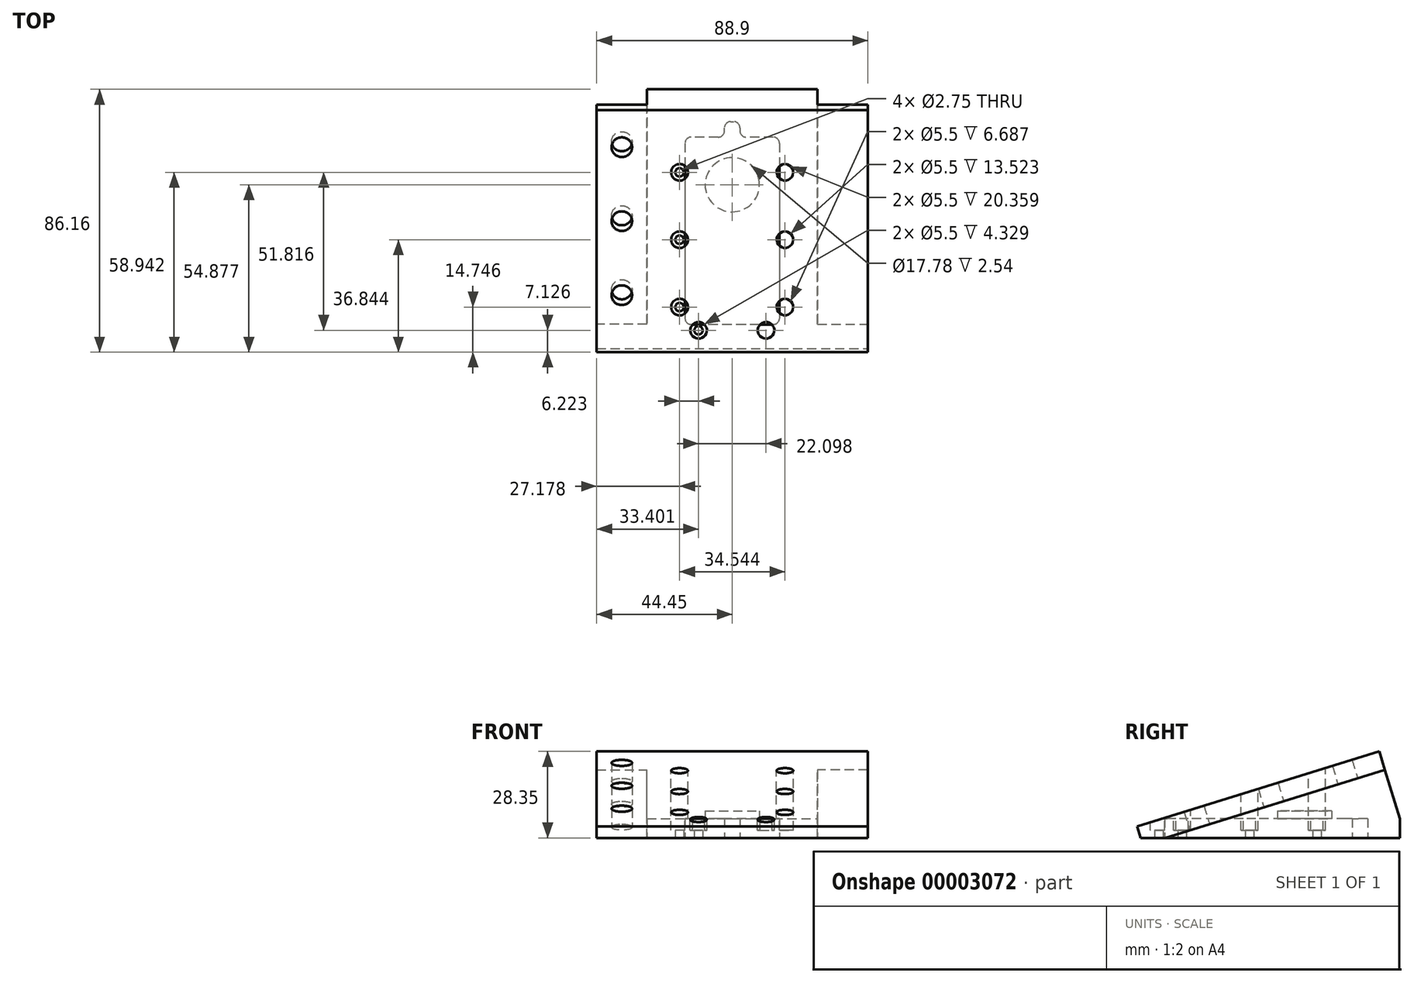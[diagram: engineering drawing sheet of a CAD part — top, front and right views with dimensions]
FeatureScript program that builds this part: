
annotation { "Feature Type Name" : "Feature", "Feature Type Description" : "" }
export const myFeature = defineFeature(function(context is Context, id is Id, definition is map)
    precondition{}
    {
        {
            var Q0;
            Q0=qCreatedBy(makeId("Top.planeOp"),FACE);
            var sketch = newSketch(context, id + "F0", { "sketchPlane" : qUnion([Q0])});
            skLineSegment(sketch, "E0.bottom", {"start": v(-44.45, 51.46) * mm, "end": v(44.45, 51.46) * mm});
            skLineSegment(sketch, "E0.top", {"start": v(-44.45, -53.4) * mm, "end": v(44.45, -53.4) * mm});
            skLineSegment(sketch, "E0.left", {"start": v(-44.45, 51.46) * mm, "end": v(-44.45, -53.4) * mm});
            skLineSegment(sketch, "E0.right", {"start": v(44.45, 51.46) * mm, "end": v(44.45, -53.4) * mm});
            skSolve(sketch);
        }
        {
            var Q0;
            Q0=makeQuery(id+"F0.imprint","IMPRINT",FACE,{"disambiguationData":[TD([[makeQuery(id+"F0.imprint","IMPRINT",EDGE,{"derivedFrom":sQuery(id+"F0.wireOp",EDGE,"E0.bottom")}),-1.0]])]});
            extrude(context, id + "F1", {"entities" : qUnion([Q0]), "depth" : 31.75 * mm});
        }
        {
            var Q0;
            Q0=qCreatedBy(makeId("Top.planeOp"),FACE);
            var sketch = newSketch(context, id + "F2", { "sketchPlane" : qUnion([Q0])});
            skLineSegment(sketch, "E1", {"start": v(0, 35.3) * mm, "end": v(0, -42.49) * mm, "construction": true});
            skLineSegment(sketch, "E2", {"start": v(-17.27, 35.58) * mm, "end": v(-17.27, -34.64) * mm, "construction": true});
            skCircle(sketch, "E3", {"center": v(-17.27, 24.24) * mm, "radius": 1.38 * mm});
            skCircle(sketch, "E4", {"center": v(-17.27, 2.14) * mm, "radius": 1.38 * mm});
            skCircle(sketch, "E5", {"center": v(-17.27, -19.95) * mm, "radius": 1.38 * mm});
            skCircle(sketch, "E6", {"center": v(0, 20.18) * mm, "radius": 3.79 * mm, "construction": true});
            skLineSegment(sketch, "E7", {"start": v(-11.05, -19.72) * mm, "end": v(-11.05, -39.28) * mm, "construction": true});
            skLineSegment(sketch, "E8", {"start": v(-15.3, -27.57) * mm, "end": v(-6, -27.57) * mm, "construction": true});
            skCircle(sketch, "E9", {"center": v(-11.05, -27.57) * mm, "radius": 1.38 * mm});
            skCircle(sketch, "E10.0.MirrorC", {"center": v(11.05, -27.57) * mm, "radius": 1.38 * mm});
            skCircle(sketch, "E11.0.MirrorC", {"center": v(17.27, -19.95) * mm, "radius": 1.38 * mm});
            skCircle(sketch, "E12.0.MirrorC", {"center": v(17.27, 2.14) * mm, "radius": 1.38 * mm});
            skCircle(sketch, "E13.0.MirrorC", {"center": v(17.27, 24.24) * mm, "radius": 1.38 * mm});
            skSolve(sketch);
        }
        {
            var Q0;
            Q0=makeQuery(id+"F2.imprint","IMPRINT",FACE,{"disambiguationData":[TD([[makeQuery(id+"F2.imprint","IMPRINT",EDGE,{"derivedFrom":sQuery(id+"F2.wireOp",EDGE,"E13.0.MirrorC")}),-1.0]])]});
            var Q1;
            Q1=makeQuery(id+"F2.imprint","IMPRINT",FACE,{"disambiguationData":[TD([[makeQuery(id+"F2.imprint","IMPRINT",EDGE,{"derivedFrom":sQuery(id+"F2.wireOp",EDGE,"E12.0.MirrorC")}),-1.0]])]});
            var Q2;
            Q2=makeQuery(id+"F2.imprint","IMPRINT",FACE,{"disambiguationData":[TD([[makeQuery(id+"F2.imprint","IMPRINT",EDGE,{"derivedFrom":sQuery(id+"F2.wireOp",EDGE,"E11.0.MirrorC")}),-1.0]])]});
            var Q3;
            Q3=makeQuery(id+"F2.imprint","IMPRINT",FACE,{"disambiguationData":[TD([[makeQuery(id+"F2.imprint","IMPRINT",EDGE,{"derivedFrom":sQuery(id+"F2.wireOp",EDGE,"E10.0.MirrorC")}),-1.0]])]});
            var Q4;
            Q4=makeQuery(id+"F2.imprint","IMPRINT",FACE,{"disambiguationData":[TD([[makeQuery(id+"F2.imprint","IMPRINT",EDGE,{"derivedFrom":sQuery(id+"F2.wireOp",EDGE,"E9")}),1.0]])]});
            var Q5;
            Q5=makeQuery(id+"F2.imprint","IMPRINT",FACE,{"disambiguationData":[TD([[makeQuery(id+"F2.imprint","IMPRINT",EDGE,{"derivedFrom":sQuery(id+"F2.wireOp",EDGE,"E5")}),1.0]])]});
            var Q6;
            Q6=makeQuery(id+"F2.imprint","IMPRINT",FACE,{"disambiguationData":[TD([[makeQuery(id+"F2.imprint","IMPRINT",EDGE,{"derivedFrom":sQuery(id+"F2.wireOp",EDGE,"E4")}),1.0]])]});
            var Q7;
            Q7=makeQuery(id+"F2.imprint","IMPRINT",FACE,{"disambiguationData":[TD([[makeQuery(id+"F2.imprint","IMPRINT",EDGE,{"derivedFrom":sQuery(id+"F2.wireOp",EDGE,"E3")}),1.0]])]});
            extrude(context, id + "F3", {"entities" : qUnion([Q0, Q1, Q2, Q3, Q4, Q5, Q6, Q7]), "operationType" : NewBodyOperationType.REMOVE, "depth" : 25.4 * mm});
        }
        {
            var Q0;
            Q0=makeQuery(id+"F1.opExtrude","CAP_FACE",FACE,{"disambiguationData":[OSD([sQuery(id+"F0.wireOp",EDGE,"E0.bottom"),sQuery(id+"F0.wireOp",EDGE,"E0.top"),sQuery(id+"F0.wireOp",EDGE,"E0.left"),sQuery(id+"F0.wireOp",EDGE,"E0.right")])],"isStart":false});
            var sketch = newSketch(context, id + "F4", { "sketchPlane" : qUnion([Q0])});
            skCircle(sketch, "E14", {"center": v(-17.27, 24.24) * mm, "radius": 2.75 * mm});
            skCircle(sketch, "E15", {"center": v(-17.27, 2.14) * mm, "radius": 2.75 * mm});
            skCircle(sketch, "E16", {"center": v(-17.27, -19.95) * mm, "radius": 2.75 * mm});
            skCircle(sketch, "E17", {"center": v(-11.05, -27.57) * mm, "radius": 2.75 * mm});
            skCircle(sketch, "E18", {"center": v(11.05, -27.57) * mm, "radius": 2.75 * mm});
            skCircle(sketch, "E19", {"center": v(17.27, -19.95) * mm, "radius": 2.75 * mm});
            skCircle(sketch, "E20", {"center": v(17.27, 2.14) * mm, "radius": 2.75 * mm});
            skCircle(sketch, "E21", {"center": v(17.27, 24.24) * mm, "radius": 2.75 * mm});
            skSolve(sketch);
        }
        {
            var Q0;
            Q0=makeQuery(id+"F4.imprint","IMPRINT",FACE,{"disambiguationData":[TD([[makeQuery(id+"F4.imprint","IMPRINT",EDGE,{"derivedFrom":sQuery(id+"F4.wireOp",EDGE,"E14")}),1.0]])]});
            var Q1;
            Q1=makeQuery(id+"F4.imprint","IMPRINT",FACE,{"disambiguationData":[TD([[makeQuery(id+"F4.imprint","IMPRINT",EDGE,{"derivedFrom":sQuery(id+"F4.wireOp",EDGE,"E15")}),1.0]])]});
            var Q2;
            Q2=makeQuery(id+"F4.imprint","IMPRINT",FACE,{"disambiguationData":[TD([[makeQuery(id+"F4.imprint","IMPRINT",EDGE,{"derivedFrom":sQuery(id+"F4.wireOp",EDGE,"E21")}),1.0]])]});
            var Q3;
            Q3=makeQuery(id+"F4.imprint","IMPRINT",FACE,{"disambiguationData":[TD([[makeQuery(id+"F4.imprint","IMPRINT",EDGE,{"derivedFrom":sQuery(id+"F4.wireOp",EDGE,"E20")}),1.0]])]});
            var Q4;
            Q4=makeQuery(id+"F4.imprint","IMPRINT",FACE,{"disambiguationData":[TD([[makeQuery(id+"F4.imprint","IMPRINT",EDGE,{"derivedFrom":sQuery(id+"F4.wireOp",EDGE,"E19")}),1.0]])]});
            var Q5;
            Q5=makeQuery(id+"F4.imprint","IMPRINT",FACE,{"disambiguationData":[TD([[makeQuery(id+"F4.imprint","IMPRINT",EDGE,{"derivedFrom":sQuery(id+"F4.wireOp",EDGE,"E18")}),1.0]])]});
            var Q6;
            Q6=makeQuery(id+"F4.imprint","IMPRINT",FACE,{"disambiguationData":[TD([[makeQuery(id+"F4.imprint","IMPRINT",EDGE,{"derivedFrom":sQuery(id+"F4.wireOp",EDGE,"E17")}),1.0]])]});
            var Q7;
            Q7=makeQuery(id+"F4.imprint","IMPRINT",FACE,{"disambiguationData":[TD([[makeQuery(id+"F4.imprint","IMPRINT",EDGE,{"derivedFrom":sQuery(id+"F4.wireOp",EDGE,"E16")}),1.0]])]});
            extrude(context, id + "F5", {"entities" : qUnion([Q0, Q1, Q2, Q3, Q4, Q5, Q6, Q7]), "operationType" : NewBodyOperationType.REMOVE, "oppositeDirection" : true, "depth" : 29.2 * mm});
        }
        {
            var Q0;
            Q0=makeQuery(id+"F1.opExtrude","CAP_FACE",FACE,{"disambiguationData":[OSD([sQuery(id+"F0.wireOp",EDGE,"E0.bottom"),sQuery(id+"F0.wireOp",EDGE,"E0.top"),sQuery(id+"F0.wireOp",EDGE,"E0.left"),sQuery(id+"F0.wireOp",EDGE,"E0.right")])],"isStart":true});
            var sketch = newSketch(context, id + "F6", { "sketchPlane" : qUnion([Q0])});
            skLineSegment(sketch, "E22.bottom", {"start": v(14.48, -34.8) * mm, "end": v(-14.48, -34.8) * mm, "construction": true});
            skLineSegment(sketch, "E22.top", {"start": v(14.48, 24.64) * mm, "end": v(-14.48, 24.64) * mm, "construction": true});
            skLineSegment(sketch, "E22.left", {"start": v(14.48, -34.8) * mm, "end": v(14.48, 24.64) * mm, "construction": true});
            skLineSegment(sketch, "E22.right", {"start": v(-14.48, -34.8) * mm, "end": v(-14.48, 24.64) * mm, "construction": true});
            skLineSegment(sketch, "E23", {"start": v(15.9, -24.38) * mm, "end": v(-15.9, -24.38) * mm, "construction": true});
            skLineSegment(sketch, "E24", {"start": v(0, -24.38) * mm, "end": v(0, 28.76) * mm, "construction": true});
            skLineSegment(sketch, "E25", {"start": v(16.02, -20.32) * mm, "end": v(-16.34, -20.32) * mm, "construction": true});
            skLineSegment(sketch, "E26.0", {"start": v(15.48, -35.8) * mm, "end": v(2.54, -35.8) * mm});
            skLineSegment(sketch, "E26.1", {"start": v(15.48, -35.8) * mm, "end": v(15.48, 25.64) * mm});
            skLineSegment(sketch, "E26.2", {"start": v(15.48, 25.64) * mm, "end": v(-15.48, 25.64) * mm});
            skLineSegment(sketch, "E26.3", {"start": v(-15.48, -35.8) * mm, "end": v(-15.48, 25.64) * mm});
            skLineSegment(sketch, "E27", {"start": v(-2.54, -35.8) * mm, "end": v(-2.54, -40.87) * mm});
            skLineSegment(sketch, "E28", {"start": v(-2.54, -40.87) * mm, "end": v(2.54, -40.87) * mm});
            skLineSegment(sketch, "E29", {"start": v(2.54, -40.87) * mm, "end": v(2.54, -35.8) * mm});
            skLineSegment(sketch, "E30.trimOffspring", {"start": v(-2.54, -35.8) * mm, "end": v(-15.48, -35.8) * mm});
            skSolve(sketch);
        }
        {
            var Q0;
            Q0=makeQuery(id+"F6.imprint","IMPRINT",FACE,{"disambiguationData":[TD([[makeQuery(id+"F6.imprint","IMPRINT",EDGE,{"derivedFrom":sQuery(id+"F6.wireOp",EDGE,"E26.0")}),-1.0]])]});
            extrude(context, id + "F7", {"entities" : qUnion([Q0]), "operationType" : NewBodyOperationType.REMOVE, "oppositeDirection" : true, "depth" : 6.35 * mm});
        }
        {
            var Q0;
            Q0=makeQuery(id+"F7.boolean.opBoolean","COPY",EDGE,{"derivedFrom":makeQuery(id+"F7.opExtrude","SWEPT_EDGE",EDGE,{"disambiguationData":[OSD([sQuery(id+"F6.wireOp",EDGE,"E26.0"),sQuery(id+"F6.wireOp",EDGE,"E26.1")])]})});
            var Q1;
            Q1=makeQuery(id+"F7.boolean.opBoolean","COPY",EDGE,{"derivedFrom":makeQuery(id+"F7.opExtrude","SWEPT_EDGE",EDGE,{"disambiguationData":[OSD([sQuery(id+"F6.wireOp",EDGE,"E26.2"),sQuery(id+"F6.wireOp",EDGE,"E26.3")])]})});
            var Q2;
            Q2=makeQuery(id+"F7.boolean.opBoolean","COPY",EDGE,{"derivedFrom":makeQuery(id+"F7.opExtrude","SWEPT_EDGE",EDGE,{"disambiguationData":[OSD([sQuery(id+"F6.wireOp",EDGE,"E26.3"),sQuery(id+"F6.wireOp",EDGE,"E30.trimOffspring")])]})});
            var Q3;
            Q3=makeQuery(id+"F7.boolean.opBoolean","COPY",EDGE,{"derivedFrom":makeQuery(id+"F7.opExtrude","SWEPT_EDGE",EDGE,{"disambiguationData":[OSD([sQuery(id+"F6.wireOp",EDGE,"E26.2"),sQuery(id+"F6.wireOp",EDGE,"E26.3")])]})});
            var Q4;
            Q4=makeQuery(id+"F7.boolean.opBoolean","COPY",EDGE,{"derivedFrom":makeQuery(id+"F7.opExtrude","SWEPT_EDGE",EDGE,{"disambiguationData":[OSD([sQuery(id+"F6.wireOp",EDGE,"E26.0"),sQuery(id+"F6.wireOp",EDGE,"E26.1")])]})});
            var Q5;
            Q5=makeQuery(id+"F7.boolean.opBoolean","COPY",EDGE,{"derivedFrom":makeQuery(id+"F7.opExtrude","SWEPT_EDGE",EDGE,{"disambiguationData":[OSD([sQuery(id+"F6.wireOp",EDGE,"E26.1"),sQuery(id+"F6.wireOp",EDGE,"E26.2")])]})});
            var Q6;
            Q6=makeQuery(id+"F7.boolean.opBoolean","COPY",EDGE,{"derivedFrom":makeQuery(id+"F7.opExtrude","SWEPT_EDGE",EDGE,{"disambiguationData":[OSD([sQuery(id+"F6.wireOp",EDGE,"E26.0"),sQuery(id+"F6.wireOp",EDGE,"E29")])]})});
            var Q7;
            Q7=makeQuery(id+"F7.boolean.opBoolean","COPY",EDGE,{"derivedFrom":makeQuery(id+"F7.opExtrude","SWEPT_EDGE",EDGE,{"disambiguationData":[OSD([sQuery(id+"F6.wireOp",EDGE,"E27"),sQuery(id+"F6.wireOp",EDGE,"E30.trimOffspring")])]})});
            var Q8;
            Q8=makeQuery(id+"F7.boolean.opBoolean","COPY",EDGE,{"derivedFrom":makeQuery(id+"F7.opExtrude","SWEPT_EDGE",EDGE,{"disambiguationData":[OSD([sQuery(id+"F6.wireOp",EDGE,"E27"),sQuery(id+"F6.wireOp",EDGE,"E28")])]})});
            var Q9;
            Q9=makeQuery(id+"F7.boolean.opBoolean","COPY",EDGE,{"derivedFrom":makeQuery(id+"F7.opExtrude","SWEPT_EDGE",EDGE,{"disambiguationData":[OSD([sQuery(id+"F6.wireOp",EDGE,"E28"),sQuery(id+"F6.wireOp",EDGE,"E29")])]})});
            fillet(context, id + "F8", {"entities" : qUnion([Q0, Q1, Q2, Q3, Q4, Q5, Q6, Q7, Q8, Q9]), "radius" : 2.03 * mm, "tangentPropagation" : true, "allowEdgeOverflow" : false});
        }
        {
            var Q0;
            Q0=makeQuery(id+"F1.opExtrude","SWEPT_FACE",FACE,{"disambiguationData":[OSD([sQuery(id+"F0.wireOp",EDGE,"E0.left")])]});
            var sketch = newSketch(context, id + "F9", { "sketchPlane" : qUnion([Q0])});
            skLineSegment(sketch, "E31.0.0", {"start": v(23.61, 6.35) * mm, "end": v(25.64, 6.35) * mm, "construction": true});
            skLineSegment(sketch, "E31.0.1", {"start": v(23.61, 0) * mm, "end": v(23.61, 6.35) * mm, "construction": true});
            skLineSegment(sketch, "E31.0.2", {"start": v(25.64, 0) * mm, "end": v(23.61, 0) * mm, "construction": true});
            skLineSegment(sketch, "E31.0.3", {"start": v(25.64, 6.35) * mm, "end": v(25.64, 0) * mm, "construction": true});
            skLineSegment(sketch, "E32", {"start": v(31.23, 0) * mm, "end": v(31.23, 6.64) * mm, "construction": true});
            skLineSegment(sketch, "E33.0.0", {"start": v(-33.76, 6.35) * mm, "end": v(-26.33, 6.35) * mm, "construction": true});
            skLineSegment(sketch, "E33.0.1", {"start": v(-33.76, 6.35) * mm, "end": v(-33.76, 0) * mm, "construction": true});
            skLineSegment(sketch, "E33.0.2", {"start": v(-33.76, 0) * mm, "end": v(23.61, 0) * mm, "construction": true});
            skLineSegment(sketch, "E33.0.4", {"start": v(22.04, 6.35) * mm, "end": v(23.61, 6.35) * mm, "construction": true});
            skLineSegment(sketch, "E33.0.5", {"start": v(22.04, 2.54) * mm, "end": v(22.04, 6.35) * mm, "construction": true});
            skLineSegment(sketch, "E33.0.6", {"start": v(22.04, 2.54) * mm, "end": v(17.87, 2.54) * mm, "construction": true});
            skLineSegment(sketch, "E33.0.7", {"start": v(17.87, 6.35) * mm, "end": v(17.87, 2.54) * mm, "construction": true});
            skLineSegment(sketch, "E33.0.8", {"start": v(-0.06, 6.35) * mm, "end": v(17.87, 6.35) * mm, "construction": true});
            skLineSegment(sketch, "E33.0.9", {"start": v(-0.06, 2.54) * mm, "end": v(-0.06, 6.35) * mm, "construction": true});
            skLineSegment(sketch, "E33.0.10", {"start": v(-0.06, 2.54) * mm, "end": v(-4.23, 2.54) * mm, "construction": true});
            skLineSegment(sketch, "E33.0.11", {"start": v(-4.23, 6.35) * mm, "end": v(-4.23, 2.54) * mm, "construction": true});
            skLineSegment(sketch, "E33.0.12", {"start": v(-22.16, 6.35) * mm, "end": v(-4.23, 6.35) * mm, "construction": true});
            skLineSegment(sketch, "E33.0.13", {"start": v(-22.16, 2.54) * mm, "end": v(-22.16, 6.35) * mm, "construction": true});
            skLineSegment(sketch, "E33.0.14", {"start": v(-22.16, 2.54) * mm, "end": v(-26.33, 2.54) * mm, "construction": true});
            skLineSegment(sketch, "E33.0.15", {"start": v(-26.33, 6.35) * mm, "end": v(-26.33, 2.54) * mm, "construction": true});
            skLineSegment(sketch, "E34", {"start": v(-33.76, 0) * mm, "end": v(-26.78, 22.57) * mm, "construction": true});
            skLineSegment(sketch, "E35", {"start": v(-26.78, 22.57) * mm, "end": v(25.64, 6.35) * mm, "construction": true});
            skLineSegment(sketch, "E36", {"start": v(-26.78, 22.57) * mm, "end": v(-56.47, 31.75) * mm, "construction": true});
            skLineSegment(sketch, "E37", {"start": v(25.64, 6.35) * mm, "end": v(53.4, -2.24) * mm, "construction": true});
            skLineSegment(sketch, "E38", {"start": v(-56.47, 31.75) * mm, "end": v(53.4, -2.24) * mm});
            skLineSegment(sketch, "E39", {"start": v(53.4, 31.75) * mm, "end": v(53.4, -2.24) * mm});
            skLineSegment(sketch, "E40", {"start": v(53.4, 31.75) * mm, "end": v(-56.47, 31.75) * mm});
            skSolve(sketch);
        }
        {
            var Q0;
            Q0=makeQuery(id+"F1.opExtrude","SWEPT_FACE",FACE,{"disambiguationData":[OSD([sQuery(id+"F0.wireOp",EDGE,"E0.right")])]});
            var sketch = newSketch(context, id + "F10", { "sketchPlane" : qUnion([Q0])});
            skLineSegment(sketch, "E41.0.0", {"start": v(51.46, 31.75) * mm, "end": v(-53.4, 31.75) * mm});
            skLineSegment(sketch, "E41.0.1", {"start": v(51.46, 30.2) * mm, "end": v(35.94, 25.4) * mm});
            skLineSegment(sketch, "E41.0.2", {"start": v(-53.4, 31.75) * mm, "end": v(-53.4, 1.07) * mm});
            skLineSegment(sketch, "E42.0", {"start": v(19.8, 20.68) * mm, "end": v(-39.5, 2.33) * mm});
            skLineSegment(sketch, "E43.0", {"start": v(57.8, -6.35) * mm, "end": v(-59.75, -6.35) * mm});
            skLineSegment(sketch, "E43.1", {"start": v(57.8, 38.1) * mm, "end": v(57.8, -6.35) * mm});
            skLineSegment(sketch, "E43.2", {"start": v(57.8, 38.1) * mm, "end": v(-59.75, 38.1) * mm});
            skLineSegment(sketch, "E43.3", {"start": v(-59.75, 38.1) * mm, "end": v(-59.75, -6.35) * mm});
            skLineSegment(sketch, "E44", {"start": v(19.8, 20.68) * mm, "end": v(55.6, 31.75) * mm});
            skLineSegment(sketch, "E45", {"start": v(-39.5, 2.33) * mm, "end": v(-53.4, -1.97) * mm});
            skSolve(sketch);
        }
        {
            var Q0;
            Q0=makeQuery(id+"F10.imprint","IMPRINT",FACE,{"disambiguationData":[TD([[makeQuery(id+"F10.imprint","IMPRINT",EDGE,{"derivedFrom":sQuery(id+"F10.wireOp",EDGE,"E42.0")}),-1.0]])]});
            extrude(context, id + "F11", {"entities" : qUnion([Q0]), "operationType" : NewBodyOperationType.REMOVE, "endBound" : BoundingType.THROUGH_ALL, "oppositeDirection" : true, "depth" : 25.4 * mm});
        }
        {
            var Q0;
            Q0=makeQuery(id+"F1.opExtrude","SWEPT_FACE",FACE,{"disambiguationData":[OSD([sQuery(id+"F0.wireOp",EDGE,"E0.left")])]});
            var sketch = newSketch(context, id + "F12", { "sketchPlane" : qUnion([Q0])});
            skLineSegment(sketch, "E46", {"start": v(25.54, 0) * mm, "end": v(-51.46, 23.82) * mm});
            skLineSegment(sketch, "E47", {"start": v(-51.46, 23.82) * mm, "end": v(-51.46, 0) * mm});
            skLineSegment(sketch, "E48", {"start": v(-51.46, 0) * mm, "end": v(25.54, 0) * mm});
            skSolve(sketch);
        }
        {
            var Q0;
            Q0=makeQuery(id+"F12.imprint","IMPRINT",FACE,{"disambiguationData":[TD([[makeQuery(id+"F12.imprint","IMPRINT",EDGE,{"derivedFrom":sQuery(id+"F12.wireOp",EDGE,"E46")}),1.0]])]});
            extrude(context, id + "F13", {"entities" : qUnion([Q0]), "operationType" : NewBodyOperationType.REMOVE, "oppositeDirection" : true, "depth" : 16.5 * mm});
        }
        {
            var Q0;
            Q0=makeQuery(id+"F1.opExtrude","SWEPT_FACE",FACE,{"disambiguationData":[OSD([sQuery(id+"F0.wireOp",EDGE,"E0.right")])]});
            var sketch = newSketch(context, id + "F14", { "sketchPlane" : qUnion([Q0])});
            skLineSegment(sketch, "E49.0.0", {"start": v(51.46, 0) * mm, "end": v(-25.54, 0) * mm});
            skLineSegment(sketch, "E49.0.1", {"start": v(-25.54, 0) * mm, "end": v(51.46, 23.82) * mm});
            skLineSegment(sketch, "E49.0.2", {"start": v(51.46, 23.82) * mm, "end": v(51.46, 0) * mm});
            skSolve(sketch);
        }
        {
            var Q0;
            Q0=makeQuery(id+"F14.imprint","IMPRINT",FACE,{"disambiguationData":[TD([[makeQuery(id+"F14.imprint","IMPRINT",EDGE,{"derivedFrom":sQuery(id+"F14.wireOp",EDGE,"E49.0.0")}),-1.0]])]});
            extrude(context, id + "F15", {"entities" : qUnion([Q0]), "operationType" : NewBodyOperationType.REMOVE, "oppositeDirection" : true, "depth" : 16.5 * mm});
        }
        {
            var Q0;
            Q0=makeQuery(id+"F1.opExtrude","SWEPT_FACE",FACE,{"disambiguationData":[OSD([sQuery(id+"F0.wireOp",EDGE,"E0.right")])]});
            var sketch = newSketch(context, id + "F16", { "sketchPlane" : qUnion([Q0])});
            skLineSegment(sketch, "E50", {"start": v(-25.54, 0) * mm, "end": v(-27.42, 6.07) * mm, "construction": true});
            skLineSegment(sketch, "E51", {"start": v(-34.7, 3.81) * mm, "end": v(-33.52, 0) * mm});
            skLineSegment(sketch, "E52.0.0", {"start": v(-25.54, 0) * mm, "end": v(51.46, 23.82) * mm, "construction": true});
            skLineSegment(sketch, "E52.0.1", {"start": v(51.46, 0) * mm, "end": v(-25.54, 0) * mm, "construction": true});
            skLineSegment(sketch, "E52.0.2", {"start": v(51.46, 23.82) * mm, "end": v(51.46, 0) * mm, "construction": true});
            skLineSegment(sketch, "E53", {"start": v(44.63, 28.35) * mm, "end": v(51.46, 6.27) * mm});
            skLineSegment(sketch, "E54", {"start": v(51.46, 6.27) * mm, "end": v(51.46, 30.47) * mm});
            skLineSegment(sketch, "E55", {"start": v(51.46, 30.47) * mm, "end": v(44.63, 28.35) * mm});
            skSolve(sketch);
        }
        {
            var Q0;
            {var subQ1=sQuery(id+"F16.wireOp",EDGE,"E51");Q0=makeQuery(id+"F16.imprint","IMPRINT",FACE,{"disambiguationData":[TD([[makeQuery(id+"F16.imprint","IMPRINT",EDGE,{"derivedFrom":subQ1}),-1.0]])]});}
            var Q1;
            {var subQ5=sQuery(id+"F16.wireOp",EDGE,"E55");Q1=makeQuery(id+"F16.imprint","IMPRINT",FACE,{"disambiguationData":[TD([[makeQuery(id+"F16.imprint","IMPRINT",EDGE,{"derivedFrom":subQ5}),1.0]])]});}
            var Q2;
            {var subQ1=sQuery(id+"F16.wireOp",EDGE,"E53");var subQ3=sQuery(id+"F16.wireOp",EDGE,"E54");var subQ5=makeQuery(id+"F16.imprint","INTERSECT",VERTEX,{"derivedFrom":[subQ1,subQ3]});Q2=makeQuery(id+"F16.imprint","IMPRINT",FACE,{"disambiguationData":[TD([[makeQuery(id+"F16.imprint","IMPRINT",EDGE,{"disambiguationData":[TD([[subQ5,1.0]])],"derivedFrom":subQ1}),1.0]])]});}
            extrude(context, id + "F17", {"entities" : qUnion([Q0, Q1, Q2]), "operationType" : NewBodyOperationType.REMOVE, "endBound" : BoundingType.THROUGH_ALL, "oppositeDirection" : true, "depth" : 25.4 * mm});
        }
        {
            var Q0;
            Q0=makeQuery(id+"F13.boolean.opBoolean","COPY",FACE,{"derivedFrom":makeQuery(id+"F13.opExtrude","SWEPT_FACE",FACE,{"disambiguationData":[OSD([sQuery(id+"F12.wireOp",EDGE,"E46")])]})});
            var sketch = newSketch(context, id + "F18", { "sketchPlane" : qUnion([Q0])});
            skLineSegment(sketch, "E56", {"start": v(0, -2.48) * mm, "end": v(0, -48.58) * mm, "construction": true});
            skLineSegment(sketch, "E57", {"start": v(-36.2, 24.4) * mm, "end": v(-36.2, -51.01) * mm, "construction": true});
            skCircle(sketch, "E58", {"center": v(-36.2, 12.49) * mm, "radius": 3.38 * mm});
            skCircle(sketch, "E59", {"center": v(-36.2, -12.91) * mm, "radius": 3.38 * mm});
            skCircle(sketch, "E60", {"center": v(-36.2, -38.31) * mm, "radius": 3.38 * mm});
            skCircle(sketch, "E61.0.MirrorC", {"center": v(36.2, -38.31) * mm, "radius": 3.38 * mm});
            skCircle(sketch, "E61.1.MirrorC", {"center": v(36.2, -12.91) * mm, "radius": 3.38 * mm});
            skCircle(sketch, "E61.2.MirrorC", {"center": v(36.2, 12.49) * mm, "radius": 3.38 * mm});
            skSolve(sketch);
        }
        {
            var Q0;
            Q0=makeQuery(id+"F18.imprint","IMPRINT",FACE,{"disambiguationData":[TD([[makeQuery(id+"F18.imprint","IMPRINT",EDGE,{"derivedFrom":sQuery(id+"F18.wireOp",EDGE,"E58")}),1.0]])]});
            var Q1;
            Q1=makeQuery(id+"F18.imprint","IMPRINT",FACE,{"disambiguationData":[TD([[makeQuery(id+"F18.imprint","IMPRINT",EDGE,{"derivedFrom":sQuery(id+"F18.wireOp",EDGE,"E60")}),1.0]])]});
            var Q2;
            Q2=makeQuery(id+"F18.imprint","IMPRINT",FACE,{"disambiguationData":[TD([[makeQuery(id+"F18.imprint","IMPRINT",EDGE,{"derivedFrom":sQuery(id+"F18.wireOp",EDGE,"E61.0.MirrorC")}),-1.0]])]});
            var Q3;
            Q3=makeQuery(id+"F18.imprint","IMPRINT",FACE,{"disambiguationData":[TD([[makeQuery(id+"F18.imprint","IMPRINT",EDGE,{"derivedFrom":sQuery(id+"F18.wireOp",EDGE,"E61.1.MirrorC")}),-1.0]])]});
            var Q4;
            Q4=makeQuery(id+"F18.imprint","IMPRINT",FACE,{"disambiguationData":[TD([[makeQuery(id+"F18.imprint","IMPRINT",EDGE,{"derivedFrom":sQuery(id+"F18.wireOp",EDGE,"E61.2.MirrorC")}),-1.0]])]});
            var Q5;
            Q5=makeQuery(id+"F18.imprint","IMPRINT",FACE,{"disambiguationData":[TD([[makeQuery(id+"F18.imprint","IMPRINT",EDGE,{"derivedFrom":sQuery(id+"F18.wireOp",EDGE,"E59")}),1.0]])]});
            extrude(context, id + "F19", {"entities" : qUnion([Q0, Q1, Q2, Q3, Q4, Q5]), "operationType" : NewBodyOperationType.REMOVE, "endBound" : BoundingType.THROUGH_ALL, "oppositeDirection" : true, "depth" : 25.4 * mm});
        }
        {
            var Q0;
            Q0=makeQuery(id+"F7.boolean.opBoolean","COPY",FACE,{"derivedFrom":makeQuery(id+"F7.opExtrude","CAP_FACE",FACE,{"disambiguationData":[OSD([sQuery(id+"F6.wireOp",EDGE,"E26.0"),sQuery(id+"F6.wireOp",EDGE,"E26.1"),sQuery(id+"F6.wireOp",EDGE,"E26.2"),sQuery(id+"F6.wireOp",EDGE,"E26.3"),sQuery(id+"F6.wireOp",EDGE,"E27"),sQuery(id+"F6.wireOp",EDGE,"E28"),sQuery(id+"F6.wireOp",EDGE,"E29"),sQuery(id+"F6.wireOp",EDGE,"E30.trimOffspring")])],"isStart":false})});
            var sketch = newSketch(context, id + "F20", { "sketchPlane" : qUnion([Q0])});
            skLineSegment(sketch, "E62", {"start": v(0, 0) * mm, "end": v(0, -36.99) * mm, "construction": true});
            skCircle(sketch, "E63", {"center": v(0, -20.18) * mm, "radius": 8.9 * mm});
            skLineSegment(sketch, "E64.0.0", {"start": v(-44.45, 33.52) * mm, "end": v(44.45, 33.52) * mm});
            skLineSegment(sketch, "E64.0.1", {"start": v(-44.45, 25.54) * mm, "end": v(-44.45, 33.52) * mm});
            skLineSegment(sketch, "E64.0.2", {"start": v(-27.94, 25.54) * mm, "end": v(-44.45, 25.54) * mm});
            skLineSegment(sketch, "E64.0.3", {"start": v(-27.94, -51.46) * mm, "end": v(-27.94, 25.54) * mm});
            skLineSegment(sketch, "E64.0.4", {"start": v(-27.94, -51.46) * mm, "end": v(27.94, -51.46) * mm});
            skLineSegment(sketch, "E64.0.5", {"start": v(27.94, -51.46) * mm, "end": v(27.94, 25.54) * mm});
            skLineSegment(sketch, "E64.0.6", {"start": v(27.94, 25.54) * mm, "end": v(44.45, 25.54) * mm});
            skLineSegment(sketch, "E64.0.7", {"start": v(44.45, 25.54) * mm, "end": v(44.45, 33.52) * mm});
            skCircle(sketch, "E65", {"center": v(17.27, -24.24) * mm, "radius": 4.39 * mm, "construction": true});
            skSolve(sketch);
        }
        {
            var Q0;
            Q0=makeQuery(id+"F20.imprint","IMPRINT",FACE,{"disambiguationData":[TD([[makeQuery(id+"F20.imprint","IMPRINT",EDGE,{"derivedFrom":sQuery(id+"F20.wireOp",EDGE,"E63")}),1.0]])]});
            extrude(context, id + "F21", {"entities" : qUnion([Q0]), "operationType" : NewBodyOperationType.REMOVE, "oppositeDirection" : true, "depth" : 2.54 * mm});
        }
    });
